# Revit family: LAMP_KOMBIC 100 ROUND IP40 CRI80 OPAL
name_source: partatom
category: Luminarias
revit_build: Autodesk Revit 2018 (Build: 20190510_1515(x64)
units: mm (PartAtom-declared; Revit-internal decimal feet)

## family parameters
Anfitrión = Cara
Compartido = No
Corte con vacíos al cargar = No
Cota de conector redondo = Diámetro de uso
Origen de luz = Sí
Punto de cálculo de habitación = No
Tipo de pieza = Normal

## types (24) — shared parameters
CRI = 80
Cambio de temperatura de color de luz atenuada = <Ninguno>
Diameter = 99 mm  [stored 0.324803 ft]
Elevación por defecto = 1219 mm
Fabricante = LAMP
Filtro de color = 16777215
Gear = Electronic
Height = 75 mm
IEE = A+
Installation instructions = https://www.lamp.es
Insulation class = II
LED Lifetime = 50.000 L80 B10
Lamp = COB LED
Last update = 01/07/2021
Luminaire type = Downlight
MacAdam = 3
Manufacturer URL = http://www.lamp.es
Manufacturer country = Spain
Manufacturer name = LAMP
Material aro = LAMP_Plástico genérico BL
Material difusor = LAMP_PMMA Difusor Kombic
Material disipador = LAMP_Aluminio Disipador Kombic
Power Supply = 220-240V 50/60Hz
Product URL = https://www.lamp.es
Product datasheet = http://www.lamp.es
Protection rating = IP40
Recessed diameter = 95 mm
Type = COB PHILIPS

## per-type parameters (varying)
| type | Archivo de red fotométrica | Efficacy | Finish | Material reflector | Modelo | Plum | Power | Product code | Weight | Ángulo de inclinación |
| 1392LM 3000K DALI M/W | K11RD2040OP830nMW.IES | 104 lm/W | Shiny white RAL 9010 | LAMP_PC Reflector Kombic Metalizado Mate | K11RD2040OP830DMW | 13 W | 12 W | K11RD2040OP830DMW | 0.43 kg | -90.00° |
| 1392LM 3000K  M/W | K11RD2040OP830NMW.IES | 104 lm/W | Shiny white RAL 9010 | LAMP_PC Reflector Kombic Metalizado Mate | K11RD2040OP830NMW | 13 W | 12 W | K11RD2040OP830NMW | 0.39 kg | -90.00° |
| 1454LM 3000K DALI W/W | K11RD2040OP830nWW.IES | 109 lm/W | Matte white RAL 9010 | LAMP_PC Reflector Kombic Blanco | K11RD2040OP830DWW | 13 W | 12 W | K11RD2040OP830DWW | 0.43 kg | 90.00° |
| 1454LM 3000K  W/W | K11RD2040OP830NWW.IES | 109 lm/W | Matte white RAL 9010 | LAMP_PC Reflector Kombic Blanco | K11RD2040OP830NWW | 13 W | 12 W | K11RD2040OP830NWW | 0.39 kg | -90.00° |
| 1460LM 3000K DALI BR/W | K11RD2040OP830nRW.IES | 109 lm/W | Shiny white RAL 9010 | LAMP_PC Reflector Kombic Metalizado Brillante | K11RD2040OP830DRW | 13 W | 12 W | K11RD2040OP830DRW | 0.43 kg | -90.00° |
| 1460LM 3000K  BR/W | K11RD2040OP830NRW.IES | 109 lm/W | Shiny white RAL 9010 | LAMP_PC Reflector Kombic Metalizado Brillante | K11RD2040OP830NRW | 13 W | 12 W | K11RD2040OP830NRW | 0.39 kg | -90.00° |
| 1474LM 4000K DALI M/W | K11RD2040OP840nMW.IES | 110 lm/W | Shiny white RAL 9010 | LAMP_PC Reflector Kombic Metalizado Mate | K11RD2040OP840DMW | 13 W | 12 W | K11RD2040OP840DMW | 0.43 kg | -90.00° |
| 1474LM 4000K  M/W | K11RD2040OP840NMW.IES | 110 lm/W | Shiny white RAL 9010 | LAMP_PC Reflector Kombic Metalizado Mate | K11RD2040OP840NMW | 13 W | 12 W | K11RD2040OP840NMW | 0.39 kg | -90.00° |
| 1541LM 4000K DALI W/W | K11RD2040OP840nWW.IES | 115 lm/W | Matte white RAL 9010 | LAMP_PC Reflector Kombic Blanco | K11RD2040OP840DWW | 13 W | 12 W | K11RD2040OP840DWW | 0.43 kg | -90.00° |
| 1541LM 4000K  W/W | K11RD2040OP840NWW.IES | 115 lm/W | Matte white RAL 9010 | LAMP_PC Reflector Kombic Blanco | K11RD2040OP840NWW | 13 W | 12 W | K11RD2040OP840NWW | 0.39 kg | -90.00° |
| 1547LM 4000K DALI BR/W | K11RD2040OP840nRW.IES | 115 lm/W | Shiny white RAL 9010 | LAMP_PC Reflector Kombic Metalizado Brillante | K11RD2040OP840DRW | 13 W | 12 W | K11RD2040OP840DRW | 0.43 kg | -90.00° |
| 1547LM 4000K  BR/W | K11RD2040OP840NRW.IES | 115 lm/W | Shiny white RAL 9010 | LAMP_PC Reflector Kombic Metalizado Brillante | K11RD2040OP840NRW | 13 W | 12 W | K11RD2040OP840NRW | 0.39 kg | -90.00° |
| 1867LM 3000K DALI M/W | K11RD2540OP830nMW.IES | 98 lm/W | Shiny white RAL 9010 | LAMP_PC Reflector Kombic Metalizado Mate | K11RD2540OP830DMW | 19 W | 17 W | K11RD2540OP830DMW | 0.43 kg | -90.00° |
| 1867LM 3000K  M/W | K11RD2540OP830NMW.IES | 98 lm/W | Shiny white RAL 9010 | LAMP_PC Reflector Kombic Metalizado Mate | K11RD2540OP830NMW | 19 W | 17 W | K11RD2540OP830NMW | 0.39 kg | -90.00° |
| 1951LM 3000K DALI W/W | K11RD2540OP830nWW.IES | 102 lm/W | Matte white RAL 9010 | LAMP_PC Reflector Kombic Blanco | K11RD2540OP830DWW | 19 W | 17 W | K11RD2540OP830DWW | 0.43 kg | -90.00° |
| 1951LM 3000K  W/W | K11RD2540OP830NWW.IES | 102 lm/W | Matte white RAL 9010 | LAMP_PC Reflector Kombic Blanco | K11RD2540OP830NWW | 19 W | 17 W | K11RD2540OP830NWW | 0.39 kg | -90.00° |
| 1959LM 3000K DALI BR/W | K11RD2540OP830nRW.IES | 103 lm/W | Shiny white RAL 9010 | LAMP_PC Reflector Kombic Metalizado Brillante | K11RD2540OP830DRW | 19 W | 17 W | K11RD2540OP830DRW | 0.43 kg | -90.00° |
| 1959LM 3000K  BR/W | K11RD2540OP830NRW.IES | 103 lm/W | Shiny white RAL 9010 | LAMP_PC Reflector Kombic Metalizado Brillante | K11RD2540OP830NRW | 19 W | 17 W | K11RD2540OP830NRW | 0.39 kg | -90.00° |
| 1978LM 4000K DALI M/W | K11RD2540OP840nMW.IES | 104 lm/W | Shiny white RAL 9010 | LAMP_PC Reflector Kombic Metalizado Mate | K11RD2540OP840DMW | 19 W | 17 W | K11RD2540OP840DMW | 0.43 kg | -90.00° |
| 1978LM 4000K  M/W | K11RD2540OP840NMW.IES | 104 lm/W | Shiny white RAL 9010 | LAMP_PC Reflector Kombic Metalizado Mate | K11RD2540OP840NMW | 19 W | 17 W | K11RD2540OP840NMW | 0.39 kg | -90.00° |
| 2067LM 4000K DALI W/W | K11RD2540OP840nWW.IES | 108 lm/W | Matte white RAL 9010 | LAMP_PC Reflector Kombic Blanco | K11RD2540OP840DWW | 19 W | 17 W | K11RD2540OP840DWW | 0.43 kg | -90.00° |
| 2067LM 4000K  W/W | K11RD2540OP840NWW.IES | 108 lm/W | Matte white RAL 9010 | LAMP_PC Reflector Kombic Blanco | K11RD2540OP840NWW | 19 W | 17 W | K11RD2540OP840NWW | 0.39 kg | -90.00° |
| 2082LM 4000K DALI BR/W | K11RD2540OP840nRW.IES | 109 lm/W | Shiny white RAL 9010 | LAMP_PC Reflector Kombic Metalizado Brillante | K11RD2540OP840DRW | 19 W | 17 W | K11RD2540OP840DRW | 0.43 kg | -90.00° |
| 2082LM 4000K  BR/W | K11RD2540OP840NRW.IES | 109 lm/W | Shiny white RAL 9010 | LAMP_PC Reflector Kombic Metalizado Brillante | K11RD2540OP840NRW | 19 W | 17 W | K11RD2540OP840NRW | 0.39 kg | -90.00° |

note: [stored X ft] marks values corroborated as IEEE doubles in the binary element streams (Revit-internal decimal feet)
